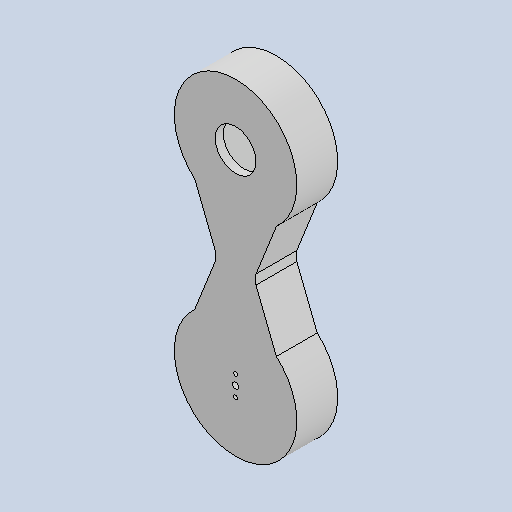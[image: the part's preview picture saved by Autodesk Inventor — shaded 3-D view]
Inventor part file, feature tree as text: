
AUTODESK INVENTOR PART (.ipt)
format: ipt  version: 2022 (Build 260153000, 153)  size: 242,176 bytes
history: native  units: in
note: dims shown in document units (in); Inventor stores cm internally (conversion verified against a paired STEP export)
features: extrude x12, sketch x12, thread x4, chamfer x1
ambient origin geometry x8: Origin, YZ Plane, XZ Plane, XY Plane, X Axis, Y Axis, Z Axis, Center Point
bodies: Solid1 (feature_tree)
feature tree (29):
  extrude  "Extrusion1"  Depth=2.3622in
  extrude  "Extrusion2"  Depth=0.7874in TaperAngle=0.0deg
  extrude  "Extrusion3"  Depth=0.6299in TaperAngle=0.0deg
  extrude  "Extrusion4"  Depth=0.0787in
  extrude  "Extrusion5"  Depth=0.0787in TaperAngle=0.0deg
  extrude  "Extrusion6"  Depth=1.1811in
  extrude  "Extrusion7"  Depth=0.3937in
  extrude  "Extrusion8"  Depth=0.2992in
  extrude  "Extrusion9"  Depth=0.2992in
  extrude  "Extrusion10"  Depth=0.1969in
  extrude  "Extrusion11"  Depth=0.1969in
  chamfer  "Chamfer2"  Distance=0.3937in
  thread  "Thread5"  [1 undecoded]
  thread  "Thread6"  [1 undecoded]
  thread  "Thread7"  [1 undecoded]
  thread  "Thread8"  [1 undecoded]
  extrude  "Extrusion12"  Depth=0.3937in
  sketch  "Sketch1"  dims[d0=2.3622in d1=2.3622in]
  sketch  "Sketch2"  dims[d2=1.5748in d3=0.7874in d4=0.0in]
  sketch  "Sketch3"  dims[d5=0.7874in d6=0.6299in d7=0.0in]
  sketch  "Sketch4"  dims[d11=0.0787in d12=0.0787in]
  sketch  "Sketch5"  dims[d13=0.0787in d14=1.1201in d15=0.0in]
  sketch  "Sketch6"  dims[d16=0.3937in d17=1.1811in]
  sketch  "Sketch7"  dims[d18=0.3937in d19=0.4134in]
  sketch  "Sketch8"  dims[d20=0.6299in d21=0.0in d22=0.2992in]
  sketch  "Sketch9"  dims[d23=0.2992in d24=0.1614in]
  sketch  "Sketch10"  dims[d25=0.1614in d26=0.1969in]
  sketch  "Sketch11"  dims[d27=0.1969in d28=0.1969in]
  sketch  "Sketch12"  dims[d29=0.1969in d30=0.3937in d31=0.0in d32=0.1614in d33=0.1614in d34=0.1969in d35=0.1969in d36=0.1063in d37=0.1063in d38=0.1063in d39=0.1063in d40=0.315in d41=0.0in d50=0.7874in d51=0.1575in d52=0.0in d53=0.7874in d54=1.1811in d55=1.1811in d56=2.8425in d57=0.0in d58=0.7874in d59=0.0in d60=0.7874in d61=0.6299in d62=0.0in d63=0.0787in d64=0.0787in d65=0.8701in d66=0.0in d67=0.4724in d68=0.0787in d69=45.0deg d70=0.315in d71=0.0in d72=0.315in d73=0.0in d74=0.315in d75=0.0in d76=0.315in d77=0.0in d78=0.1181in d79=0.3937in d80=0.0in d42=0.0197in d43=0.0344in]
note: 4 required parameter values undecoded (feature->parameter linkage not recoverable at this tier; creation-order binding heuristic only, values carry confidence <= 0.55)
